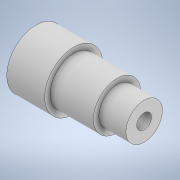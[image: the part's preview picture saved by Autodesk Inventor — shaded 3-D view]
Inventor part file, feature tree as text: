
AUTODESK INVENTOR PART (.ipt)
format: ipt  version: 2021 (Build 250183000, 183)  size: 127,488 bytes
history: native  units: mm
features: other x2, sketch x2, extrude x1
ambient origin geometry x8: Origin, YZ Plane, XZ Plane, XY Plane, X Axis, Y Axis, Z Axis, Center Point
bodies: Body1 (feature_tree)
feature tree (5):
  other  "Sólido1"
  other  "Revolução1"
  extrude  "Extrusão1"  Depth=10.0mm
  sketch  "Esboço1"  dims[d1=100.0mm d2=10.0mm]
  sketch  "Esboço3"  dims[d3=25.0mm d4=5.0mm d5=40.0mm d6=5.0mm d7=90.0deg d8=20.0mm d9=10.0mm d10=0.0mm]
